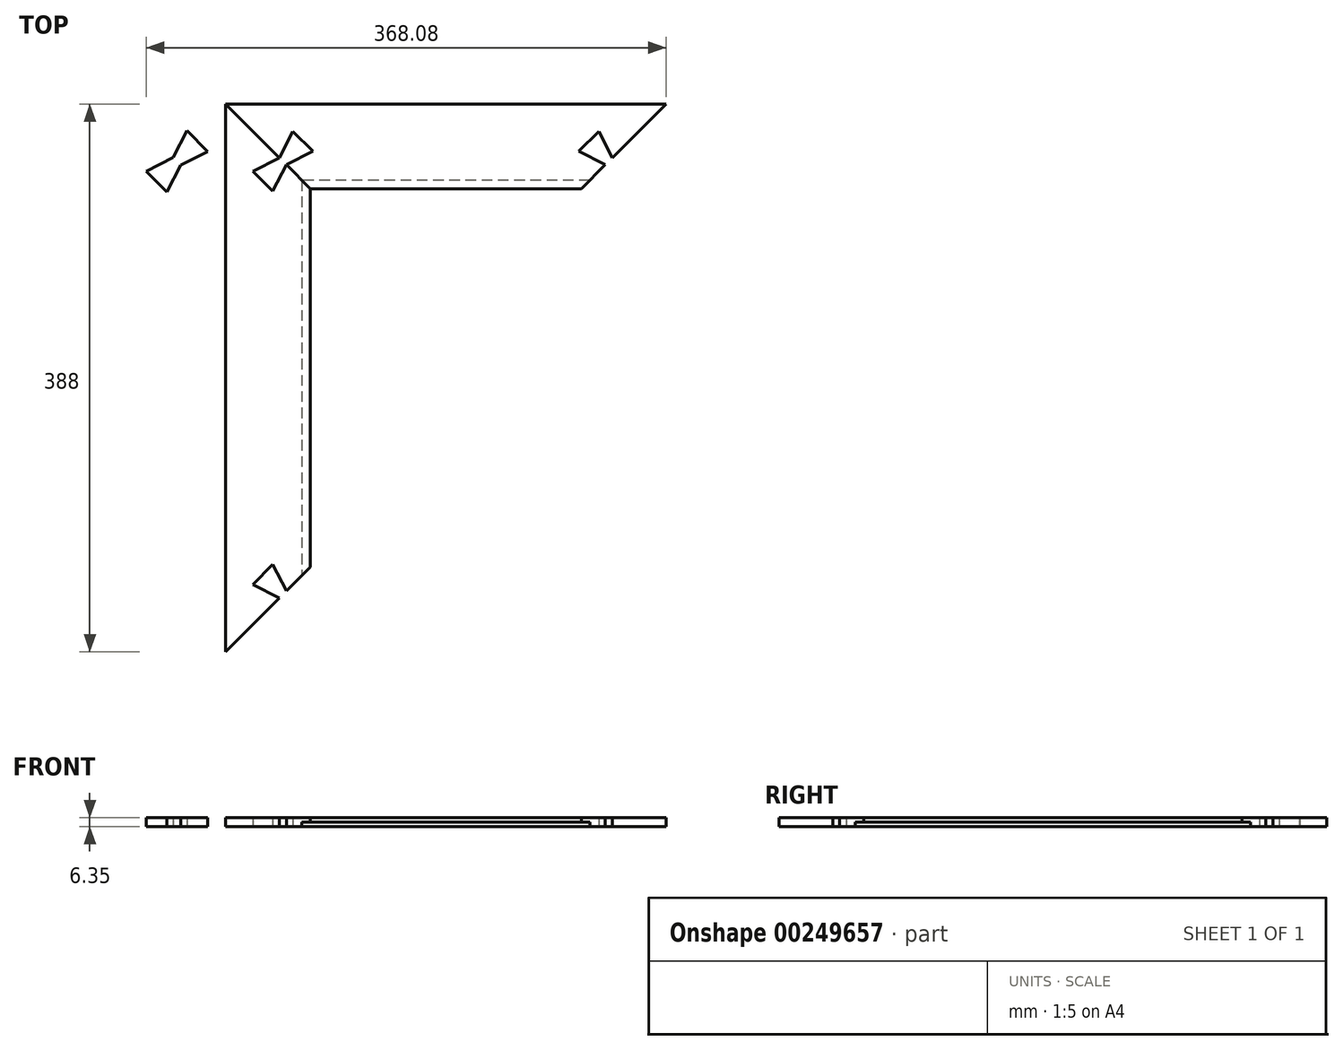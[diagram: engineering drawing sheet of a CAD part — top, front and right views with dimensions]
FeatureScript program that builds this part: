
annotation { "Feature Type Name" : "Feature", "Feature Type Description" : "" }
export const myFeature = defineFeature(function(context is Context, id is Id, definition is map)
    precondition{}
    {
        {
            assignVariable(context, id + "F0", {"name" : "BorderWidth", "anyValue" : 60});
        }
        {
            assignVariable(context, id + "F1", {"name" : "MaterialThickness", "anyValue" : 6.35});
        }
        {
            var Q0;
            Q0=qCreatedBy(makeId("Top.planeOp"),FACE);
            var sketch = newSketch(context, id + "F2", { "sketchPlane" : qUnion([Q0])});
            skLineSegment(sketch, "E0.bottom", {"start": v(96, 134) * mm, "end": v(-96, 134) * mm});
            skLineSegment(sketch, "E0.top", {"start": v(96, -134) * mm, "end": v(-96, -134) * mm});
            skLineSegment(sketch, "E0.left", {"start": v(96, 134) * mm, "end": v(96, -134) * mm});
            skLineSegment(sketch, "E0.right", {"start": v(-96, 134) * mm, "end": v(-96, -134) * mm});
            skPoint(sketch, "E0.middle", {"position": v(0, 0) * mm});
            skLineSegment(sketch, "E1.0", {"start": v(-156, 194) * mm, "end": v(-156, -194) * mm});
            skLineSegment(sketch, "E1.1", {"start": v(156, 194) * mm, "end": v(-156, 194) * mm});
            skLineSegment(sketch, "E1.2", {"start": v(156, 194) * mm, "end": v(156, -194) * mm});
            skLineSegment(sketch, "E1.3", {"start": v(156, -194) * mm, "end": v(-156, -194) * mm});
            skLineSegment(sketch, "E2", {"start": v(-96, 134) * mm, "end": v(-156, 194) * mm});
            skLineSegment(sketch, "E3", {"start": v(-117.92, 155.92) * mm, "end": v(-136.66, 146.37) * mm});
            skLineSegment(sketch, "E4", {"start": v(-136.66, 146.37) * mm, "end": v(-122.52, 132.23) * mm});
            skLineSegment(sketch, "E5", {"start": v(-122.52, 132.23) * mm, "end": v(-112.97, 150.97) * mm});
            skLineSegment(sketch, "E6", {"start": v(-112.97, 150.97) * mm, "end": v(-94.23, 160.52) * mm});
            skLineSegment(sketch, "E7", {"start": v(-94.23, 160.52) * mm, "end": v(-108.37, 174.66) * mm});
            skLineSegment(sketch, "E8", {"start": v(-108.37, 174.66) * mm, "end": v(-117.92, 155.92) * mm});
            skLineSegment(sketch, "E9.0", {"start": v(-137.08, 146.44) * mm, "end": v(-122.45, 131.81) * mm});
            skLineSegment(sketch, "E9.1", {"start": v(-112.78, 150.78) * mm, "end": v(-93.81, 160.45) * mm});
            skLineSegment(sketch, "E9.2", {"start": v(-93.81, 160.45) * mm, "end": v(-108.44, 175.08) * mm});
            skLineSegment(sketch, "E9.3", {"start": v(-122.45, 131.81) * mm, "end": v(-112.78, 150.78) * mm});
            skLineSegment(sketch, "E9.4", {"start": v(-108.44, 175.08) * mm, "end": v(-118.1, 156.1) * mm});
            skLineSegment(sketch, "E9.5", {"start": v(-118.1, 156.1) * mm, "end": v(-137.08, 146.44) * mm});
            skLineSegment(sketch, "E10", {"start": v(0, 194) * mm, "end": v(0, -194) * mm, "construction": true});
            skLineSegment(sketch, "E11", {"start": v(-156, 0) * mm, "end": v(156, 0) * mm, "construction": true});
            skLineSegment(sketch, "E12.MirrorCS", {"start": v(94.23, 160.52) * mm, "end": v(108.37, 174.66) * mm});
            skLineSegment(sketch, "E13.MirrorCS", {"start": v(137.08, 146.44) * mm, "end": v(122.45, 131.81) * mm});
            skLineSegment(sketch, "E14.MirrorCS", {"start": v(112.78, 150.78) * mm, "end": v(93.81, 160.45) * mm});
            skLineSegment(sketch, "E15.MirrorCS", {"start": v(122.45, 131.81) * mm, "end": v(112.78, 150.78) * mm});
            skLineSegment(sketch, "E16.MirrorCS", {"start": v(118.1, 156.1) * mm, "end": v(137.08, 146.44) * mm});
            skLineSegment(sketch, "E17.MirrorCS", {"start": v(112.97, 150.97) * mm, "end": v(94.23, 160.52) * mm});
            skLineSegment(sketch, "E18.MirrorCS", {"start": v(122.52, 132.23) * mm, "end": v(112.97, 150.97) * mm});
            skLineSegment(sketch, "E19.MirrorCS", {"start": v(136.66, 146.37) * mm, "end": v(122.52, 132.23) * mm});
            skLineSegment(sketch, "E20.MirrorCS", {"start": v(96, 134) * mm, "end": v(156, 194) * mm});
            skLineSegment(sketch, "E21.MirrorCS", {"start": v(108.37, 174.66) * mm, "end": v(117.92, 155.92) * mm});
            skLineSegment(sketch, "E22.MirrorCS", {"start": v(117.92, 155.92) * mm, "end": v(136.66, 146.37) * mm});
            skLineSegment(sketch, "E23.MirrorCS", {"start": v(93.81, 160.45) * mm, "end": v(108.44, 175.08) * mm});
            skLineSegment(sketch, "E24.MirrorCS", {"start": v(108.44, 175.08) * mm, "end": v(118.1, 156.1) * mm});
            skLineSegment(sketch, "E25.MirrorCS", {"start": v(-122.45, -131.81) * mm, "end": v(-112.78, -150.78) * mm});
            skLineSegment(sketch, "E26.MirrorCS", {"start": v(137.08, -146.44) * mm, "end": v(122.45, -131.81) * mm});
            skLineSegment(sketch, "E27.MirrorCS", {"start": v(94.23, -160.52) * mm, "end": v(108.37, -174.66) * mm});
            skLineSegment(sketch, "E28.MirrorCS", {"start": v(122.45, -131.81) * mm, "end": v(112.78, -150.78) * mm});
            skLineSegment(sketch, "E29.MirrorCS", {"start": v(-112.97, -150.97) * mm, "end": v(-94.23, -160.52) * mm});
            skLineSegment(sketch, "E30.MirrorCS", {"start": v(-122.52, -132.23) * mm, "end": v(-112.97, -150.97) * mm});
            skLineSegment(sketch, "E31.MirrorCS", {"start": v(-94.23, -160.52) * mm, "end": v(-108.37, -174.66) * mm});
            skLineSegment(sketch, "E32.MirrorCS", {"start": v(93.81, -160.45) * mm, "end": v(108.44, -175.08) * mm});
            skLineSegment(sketch, "E33.MirrorCS", {"start": v(96, -134) * mm, "end": v(156, -194) * mm});
            skLineSegment(sketch, "E34.MirrorCS", {"start": v(112.78, -150.78) * mm, "end": v(93.81, -160.45) * mm});
            skLineSegment(sketch, "E35.MirrorCS", {"start": v(117.92, -155.92) * mm, "end": v(136.66, -146.37) * mm});
            skLineSegment(sketch, "E36.MirrorCS", {"start": v(-93.81, -160.45) * mm, "end": v(-108.44, -175.08) * mm});
            skLineSegment(sketch, "E37.MirrorCS", {"start": v(136.66, -146.37) * mm, "end": v(122.52, -132.23) * mm});
            skLineSegment(sketch, "E38.MirrorCS", {"start": v(112.97, -150.97) * mm, "end": v(94.23, -160.52) * mm});
            skLineSegment(sketch, "E39.MirrorCS", {"start": v(108.44, -175.08) * mm, "end": v(118.1, -156.1) * mm});
            skLineSegment(sketch, "E40.MirrorCS", {"start": v(-108.44, -175.08) * mm, "end": v(-118.1, -156.1) * mm});
            skLineSegment(sketch, "E41.MirrorCS", {"start": v(108.37, -174.66) * mm, "end": v(117.92, -155.92) * mm});
            skLineSegment(sketch, "E42.MirrorCS", {"start": v(-96, -134) * mm, "end": v(-156, -194) * mm});
            skLineSegment(sketch, "E43.MirrorCS", {"start": v(-112.78, -150.78) * mm, "end": v(-93.81, -160.45) * mm});
            skLineSegment(sketch, "E44.MirrorCS", {"start": v(-118.1, -156.1) * mm, "end": v(-137.08, -146.44) * mm});
            skLineSegment(sketch, "E45.MirrorCS", {"start": v(122.52, -132.23) * mm, "end": v(112.97, -150.97) * mm});
            skLineSegment(sketch, "E46.MirrorCS", {"start": v(-136.66, -146.37) * mm, "end": v(-122.52, -132.23) * mm});
            skLineSegment(sketch, "E47.MirrorCS", {"start": v(-108.37, -174.66) * mm, "end": v(-117.92, -155.92) * mm});
            skLineSegment(sketch, "E48.MirrorCS", {"start": v(118.1, -156.1) * mm, "end": v(137.08, -146.44) * mm});
            skLineSegment(sketch, "E49.MirrorCS", {"start": v(-137.08, -146.44) * mm, "end": v(-122.45, -131.81) * mm});
            skLineSegment(sketch, "E50.MirrorCS", {"start": v(-117.92, -155.92) * mm, "end": v(-136.66, -146.37) * mm});
            skLineSegment(sketch, "E51.0", {"start": v(-102, 140) * mm, "end": v(-102, -140) * mm});
            skLineSegment(sketch, "E51.1", {"start": v(102, 140) * mm, "end": v(-102, 140) * mm});
            skLineSegment(sketch, "E51.2", {"start": v(102, 140) * mm, "end": v(102, -140) * mm});
            skLineSegment(sketch, "E51.3", {"start": v(102, -140) * mm, "end": v(-102, -140) * mm});
            skSolve(sketch);
        }
        {
            var Q0;
            {var subQ0=sQuery(id+"F2.wireOp",EDGE,"E3");Q0=makeQuery(id+"F2.imprint","IMPRINT",FACE,{"disambiguationData":[TD([[makeQuery(id+"F2.imprint","IMPRINT",EDGE,{"derivedFrom":subQ0}),1.0]])]});}
            var Q1;
            {var subQ0=sQuery(id+"F2.wireOp",EDGE,"E3");Q1=makeQuery(id+"F2.imprint","IMPRINT",FACE,{"disambiguationData":[TD([[makeQuery(id+"F2.imprint","IMPRINT",EDGE,{"derivedFrom":subQ0}),-1.0]])]});}
            var Q2;
            {var subQ2=sQuery(id+"F2.wireOp",EDGE,"E6");Q2=makeQuery(id+"F2.imprint","IMPRINT",FACE,{"disambiguationData":[TD([[makeQuery(id+"F2.imprint","IMPRINT",EDGE,{"derivedFrom":subQ2}),1.0]])]});}
            var Q3;
            {var subQ0=sQuery(id+"F2.wireOp",EDGE,"E6");Q3=makeQuery(id+"F2.imprint","IMPRINT",FACE,{"disambiguationData":[TD([[makeQuery(id+"F2.imprint","IMPRINT",EDGE,{"derivedFrom":subQ0}),-1.0]])]});}
            extrude(context, id + "F3", {"entities" : qUnion([Q0, Q1, Q2, Q3]), "depth" : (getVariable(context, 'MaterialThickness')) * mm});
        }
        {
            var Q0;
            Q0=makeQuery(id+"F3.opExtrude","SWEPT_BODY",BODY,{"disambiguationData":[OSD([sQuery(id+"F2.wireOp",EDGE,"E9.0"),sQuery(id+"F2.wireOp",EDGE,"E9.1"),sQuery(id+"F2.wireOp",EDGE,"E9.2"),sQuery(id+"F2.wireOp",EDGE,"E9.3"),sQuery(id+"F2.wireOp",EDGE,"E9.4"),sQuery(id+"F2.wireOp",EDGE,"E9.5")])]});
            transform(context, id + "F4", {"entities" : qUnion([Q0]), "transformType" : TransformType.TRANSLATION_3D, "dx" : (-getVariable(context, 'BorderWidth') * 1.25) * mm, "dy" : 0 * mm, "dz" : 0 * mm, "makeCopy" : false});
        }
        {
            var Q0;
            {var subQ1=sQuery(id+"F2.wireOp",EDGE,"E0.right");Q0=makeQuery(id+"F2.imprint","IMPRINT",FACE,{"disambiguationData":[TD([[makeQuery(id+"F2.imprint","IMPRINT",EDGE,{"derivedFrom":subQ1}),-1.0]])]});}
            var Q1;
            {var subQ0=sQuery(id+"F2.wireOp",EDGE,"E3");Q1=makeQuery(id+"F2.imprint","IMPRINT",FACE,{"disambiguationData":[TD([[makeQuery(id+"F2.imprint","IMPRINT",EDGE,{"derivedFrom":subQ0}),-1.0]])]});}
            var Q2;
            {var subQ3=sQuery(id+"F2.wireOp",EDGE,"E25.MirrorCS");Q2=makeQuery(id+"F2.imprint","IMPRINT",FACE,{"disambiguationData":[TD([[makeQuery(id+"F2.imprint","IMPRINT",EDGE,{"derivedFrom":subQ3}),-1.0]])]});}
            var Q3;
            {var subQ1=sQuery(id+"F2.wireOp",EDGE,"E1.0");Q3=makeQuery(id+"F2.imprint","IMPRINT",FACE,{"disambiguationData":[TD([[makeQuery(id+"F2.imprint","IMPRINT",EDGE,{"derivedFrom":subQ1}),1.0]])]});}
            extrude(context, id + "F5", {"entities" : qUnion([Q0, Q1, Q2, Q3]), "depth" : (getVariable(context, 'MaterialThickness')) * mm});
        }
        {
            var Q0;
            {var subQ0=sQuery(id+"F2.wireOp",EDGE,"E0.right");Q0=makeQuery(id+"F2.imprint","IMPRINT",FACE,{"disambiguationData":[TD([[makeQuery(id+"F2.imprint","IMPRINT",EDGE,{"derivedFrom":subQ0}),-1.0]])]});}
            extrude(context, id + "F6", {"entities" : qUnion([Q0]), "operationType" : NewBodyOperationType.REMOVE, "depth" : 3.17 * mm});
        }
        {
            var Q0;
            {var subQ3=sQuery(id+"F2.wireOp",EDGE,"E0.bottom");Q0=makeQuery(id+"F2.imprint","IMPRINT",FACE,{"disambiguationData":[TD([[makeQuery(id+"F2.imprint","IMPRINT",EDGE,{"derivedFrom":subQ3}),-1.0]])]});}
            var Q1;
            {var subQ0=sQuery(id+"F2.wireOp",EDGE,"E6");Q1=makeQuery(id+"F2.imprint","IMPRINT",FACE,{"disambiguationData":[TD([[makeQuery(id+"F2.imprint","IMPRINT",EDGE,{"derivedFrom":subQ0}),-1.0]])]});}
            var Q2;
            Q2=makeQuery(id+"F2.imprint","IMPRINT",FACE,{"disambiguationData":[TD([[makeQuery(id+"F2.imprint","IMPRINT",EDGE,{"derivedFrom":sQuery(id+"F2.wireOp",EDGE,"E12.MirrorCS")}),1.0]])]});
            var Q3;
            {var subQ1=sQuery(id+"F2.wireOp",EDGE,"E1.1");Q3=makeQuery(id+"F2.imprint","IMPRINT",FACE,{"disambiguationData":[TD([[makeQuery(id+"F2.imprint","IMPRINT",EDGE,{"derivedFrom":subQ1}),1.0]])]});}
            extrude(context, id + "F7", {"entities" : qUnion([Q0, Q1, Q2, Q3]), "depth" : (getVariable(context, 'MaterialThickness')) * mm});
        }
        {
            var Q0;
            {var subQ0=sQuery(id+"F2.wireOp",EDGE,"E0.bottom");Q0=makeQuery(id+"F2.imprint","IMPRINT",FACE,{"disambiguationData":[TD([[makeQuery(id+"F2.imprint","IMPRINT",EDGE,{"derivedFrom":subQ0}),-1.0]])]});}
            extrude(context, id + "F8", {"entities" : qUnion([Q0]), "operationType" : NewBodyOperationType.REMOVE, "depth" : 3.17 * mm});
        }
    });
